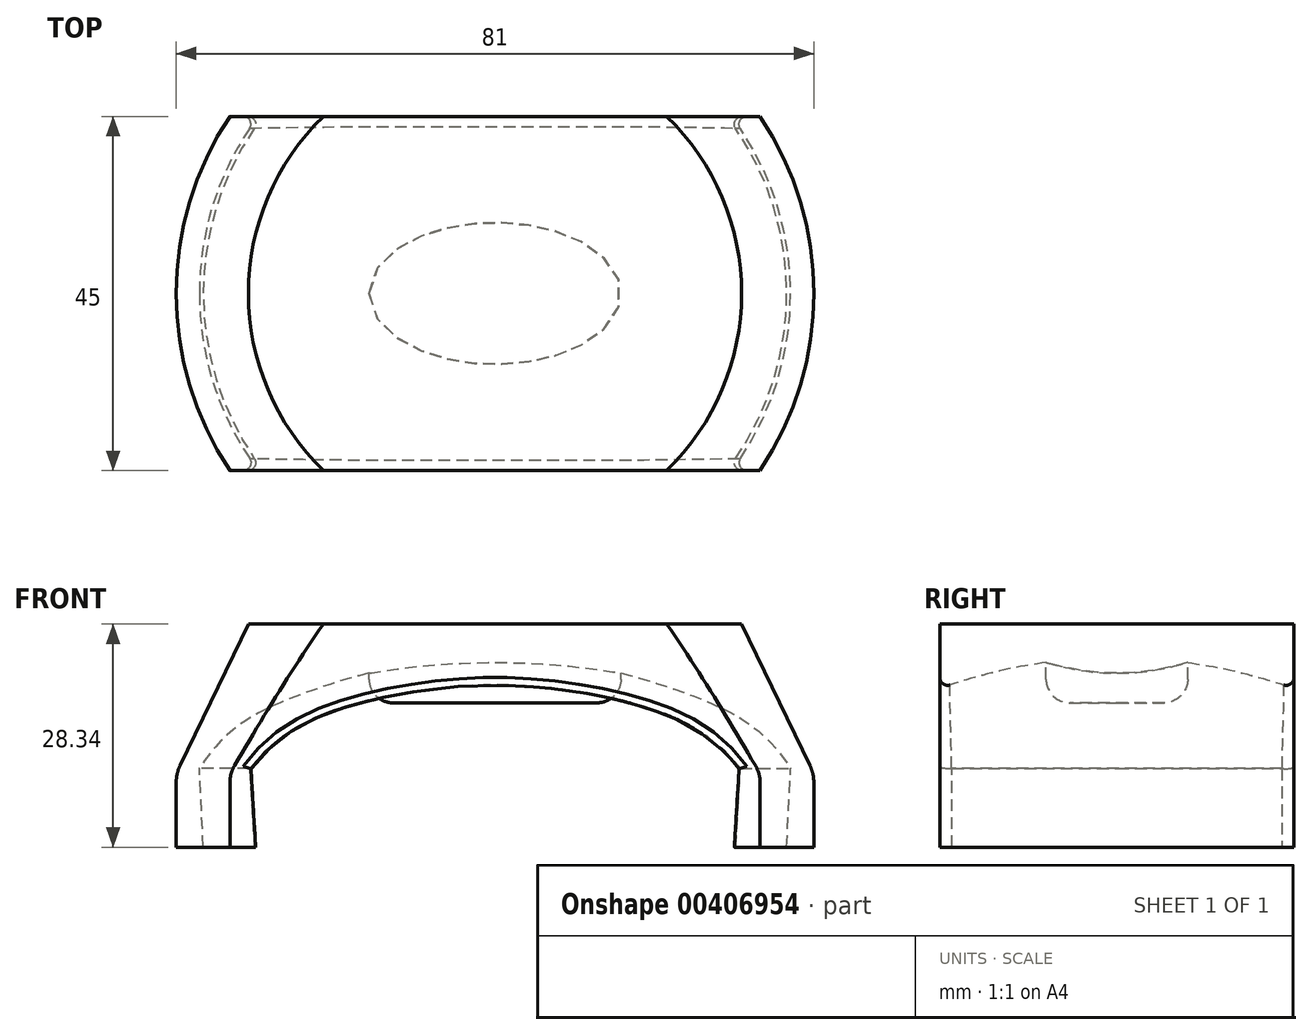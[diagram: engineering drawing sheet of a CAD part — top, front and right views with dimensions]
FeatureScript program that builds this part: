
annotation { "Feature Type Name" : "Feature", "Feature Type Description" : "" }
export const myFeature = defineFeature(function(context is Context, id is Id, definition is map)
    precondition{}
    {
        {
            var Q0;
            Q0=qCreatedBy(makeId("Top.planeOp"),FACE);
            var sketch = newSketch(context, id + "F0", { "sketchPlane" : qUnion([Q0])});
            skCircle(sketch, "E0", {"center": v(0, 0) * mm, "radius": 37.55 * mm});
            skSolve(sketch);
        }
        {
            var Q0;
            Q0=qCreatedBy(makeId("Front.planeOp"),FACE);
            var sketch = newSketch(context, id + "F1", { "sketchPlane" : qUnion([Q0])});
            skLineSegment(sketch, "E1", {"start": v(0, 0) * mm, "end": v(0, 14) * mm, "construction": true});
            skLineSegment(sketch, "E2", {"start": v(0, 0) * mm, "end": v(-37.56, 0) * mm, "construction": true});
            skFitSpline(sketch, "E3", {"points": [v(0, 14) * mm, v(-25.46, 9.08) * mm, v(-37.56, 0) * mm], "startDerivative": vector(-52.5, 1.08) * mm, "endDerivative": vector(-22.97, -35.71) * mm});
            skLineSegment(sketch, "E4", {"start": v(0, 14) * mm, "end": v(0, 18.34) * mm});
            skLineSegment(sketch, "E5", {"start": v(0, 18.34) * mm, "end": v(-31.33, 18.34) * mm});
            skLineSegment(sketch, "E6", {"start": v(-31.33, 18.34) * mm, "end": v(-40.5, -0.65) * mm});
            skLineSegment(sketch, "E7", {"start": v(-40.5, -0.65) * mm, "end": v(-40.5, -10) * mm});
            skLineSegment(sketch, "E8", {"start": v(-37.56, 0) * mm, "end": v(-37.56, -10) * mm});
            skLineSegment(sketch, "E9", {"start": v(-37.56, -10) * mm, "end": v(-37.06, -10) * mm});
            skLineSegment(sketch, "E10", {"start": v(-37.06, -10) * mm, "end": v(-37.56, 0) * mm});
            skLineSegment(sketch, "E11", {"start": v(-37.56, -10) * mm, "end": v(-40.5, -10) * mm});
            skLineSegment(sketch, "E12", {"start": v(-31.33, 18.34) * mm, "end": v(-39.17, 18.34) * mm, "construction": true});
            skSolve(sketch);
        }
        {
            var Q0;
            Q0=makeQuery(id+"F1.imprint","IMPRINT",FACE,{"disambiguationData":[TD([[makeQuery(id+"F1.imprint","IMPRINT",EDGE,{"derivedFrom":sQuery(id+"F1.wireOp",EDGE,"E3")}),-1.0]])]});
            var Q1;
            Q1=makeQuery(id+"F1.imprint","IMPRINT",FACE,{"disambiguationData":[TD([[makeQuery(id+"F1.imprint","IMPRINT",EDGE,{"derivedFrom":sQuery(id+"F1.wireOp",EDGE,"E8")}),1.0]])]});
            var Q2;
            Q2=sQuery(id+"F1.wireOp",EDGE,"E1");
            revolve(context, id + "F2", {"entities" : qUnion([Q0, Q1]), "axis" : qUnion([Q2]), "revolveType" : RevolveType.FULL});
        }
        {
            var Q0;
            Q0=qCreatedBy(makeId("Front.planeOp"),FACE);
            cPlane(context, id + "F3", {"entities" : qUnion([Q0]), "cplaneType" : CPlaneType.OFFSET, "offset" : 22.5 * mm, "width" : 150 * mm, "height" : 150 * mm});
        }
        {
            var Q0;
            Q0=qCreatedBy(id+"F3.planeOp",FACE);
            cPlane(context, id + "F4", {"entities" : qUnion([Q0]), "cplaneType" : CPlaneType.OFFSET, "offset" : 45 * mm, "oppositeDirection" : true, "width" : 150 * mm, "height" : 150 * mm});
        }
        {
            var Q0;
            Q0=qCreatedBy(id+"F3.planeOp",FACE);
            var sketch = newSketch(context, id + "F5", { "sketchPlane" : qUnion([Q0])});
            skLineSegment(sketch, "E13.bottom", {"start": v(-55.32, -24.65) * mm, "end": v(84.84, -24.65) * mm});
            skLineSegment(sketch, "E13.top", {"start": v(-55.32, 35.26) * mm, "end": v(84.84, 35.26) * mm});
            skLineSegment(sketch, "E13.left", {"start": v(-55.32, -24.65) * mm, "end": v(-55.32, 35.26) * mm});
            skLineSegment(sketch, "E13.right", {"start": v(84.84, -24.65) * mm, "end": v(84.84, 35.26) * mm});
            skSolve(sketch);
        }
        {
            var Q0;
            Q0 = qSketchRegion(id + "F5", true);
            extrude(context, id + "F6", {"entities" : qUnion([Q0]), "operationType" : NewBodyOperationType.REMOVE, "depth" : 25 * mm});
        }
        {
            var Q0;
            Q0=qCreatedBy(id+"F4.planeOp",FACE);
            var sketch = newSketch(context, id + "F7", { "sketchPlane" : qUnion([Q0])});
            skLineSegment(sketch, "E14.bottom", {"start": v(40.39, 27.93) * mm, "end": v(-45.5, 27.93) * mm});
            skLineSegment(sketch, "E14.top", {"start": v(40.39, -23.12) * mm, "end": v(-45.5, -23.12) * mm});
            skLineSegment(sketch, "E14.left", {"start": v(40.39, 27.93) * mm, "end": v(40.39, -23.12) * mm});
            skLineSegment(sketch, "E14.right", {"start": v(-45.5, 27.93) * mm, "end": v(-45.5, -23.12) * mm});
            skSolve(sketch);
        }
        {
            var Q0;
            Q0 = qSketchRegion(id + "F7", true);
            extrude(context, id + "F8", {"entities" : qUnion([Q0]), "operationType" : NewBodyOperationType.REMOVE, "oppositeDirection" : true, "depth" : 25 * mm});
        }
        {
            var Q0;
            Q0=makeQuery(id+"F2.opRevolve","SWEPT_FACE",FACE,{"disambiguationData":[OSD([sQuery(id+"F1.wireOp",EDGE,"E5")])]});
            var sketch = newSketch(context, id + "F9", { "sketchPlane" : qUnion([Q0])});
            skEllipse(sketch, "E15", {"center": v(0, 0) * mm, "majorRadius": 16 * mm, "minorRadius": 9 * mm, "majorAxis": v(-1, 0)});
            skSolve(sketch);
        }
        {
            var Q0;
            Q0=makeQuery(id+"F9.imprint","IMPRINT",FACE,{"disambiguationData":[TD([[makeQuery(id+"F9.imprint","IMPRINT",EDGE,{"derivedFrom":sQuery(id+"F9.wireOp",EDGE,"E15")}),1.0]])]});
            extrude(context, id + "F10", {"entities" : qUnion([Q0]), "operationType" : NewBodyOperationType.ADD, "oppositeDirection" : true, "depth" : 10 * mm});
        }
        {
            var Q0;
            Q0=makeQuery(id+"F10.opExtrude","CAP_EDGE",EDGE,{"disambiguationData":[OSD([sQuery(id+"F9.wireOp",EDGE,"E15")])],"isStart":false});
            fillet(context, id + "F11", {"entities" : qUnion([Q0]), "radius" : 3 * mm, "tangentPropagation" : true, "allowEdgeOverflow" : false});
        }
        {
            var Q0;
            Q0=makeQuery(id+"F8.boolean.opBoolean","SPLIT",EDGE,{"disambiguationData":[OD(0.0)],"derivedFrom":makeQuery(id+"F2.opRevolve","SWEPT_EDGE",EDGE,{"disambiguationData":[OSD([sQuery(id+"F1.wireOp",EDGE,"E6"),sQuery(id+"F1.wireOp",EDGE,"E7")])]})});
            var Q1;
            Q1=makeQuery(id+"F8.boolean.opBoolean","SPLIT",EDGE,{"disambiguationData":[OD(1.0)],"derivedFrom":makeQuery(id+"F2.opRevolve","SWEPT_EDGE",EDGE,{"disambiguationData":[OSD([sQuery(id+"F1.wireOp",EDGE,"E6"),sQuery(id+"F1.wireOp",EDGE,"E7")])]})});
            fillet(context, id + "F12", {"entities" : qUnion([Q0, Q1]), "radius" : 5 * mm, "tangentPropagation" : true, "allowEdgeOverflow" : false});
        }
        {
            var Q0;
            Q0=makeQuery(id+"F6.boolean.opBoolean","INTERSECT",EDGE,{"disambiguationData":[OD(1.0)],"derivedFrom":[makeQuery(id+"F2.opRevolve","SWEPT_FACE",FACE,{"disambiguationData":[OSD([sQuery(id+"F1.wireOp",EDGE,"E10")])]}),makeQuery(id+"F6.opExtrude","CAP_FACE",FACE,{"disambiguationData":[OSD([sQuery(id+"F5.wireOp",EDGE,"E13.bottom"),sQuery(id+"F5.wireOp",EDGE,"E13.top"),sQuery(id+"F5.wireOp",EDGE,"E13.left"),sQuery(id+"F5.wireOp",EDGE,"E13.right")])],"isStart":true})]});
            var Q1;
            Q1=makeQuery(id+"F6.boolean.opBoolean","INTERSECT",EDGE,{"disambiguationData":[OD(0.0)],"derivedFrom":[makeQuery(id+"F2.opRevolve","SWEPT_FACE",FACE,{"disambiguationData":[OSD([sQuery(id+"F1.wireOp",EDGE,"E10")])]}),makeQuery(id+"F6.opExtrude","CAP_FACE",FACE,{"disambiguationData":[OSD([sQuery(id+"F5.wireOp",EDGE,"E13.bottom"),sQuery(id+"F5.wireOp",EDGE,"E13.top"),sQuery(id+"F5.wireOp",EDGE,"E13.left"),sQuery(id+"F5.wireOp",EDGE,"E13.right")])],"isStart":true})]});
            var Q2;
            Q2=makeQuery(id+"F8.boolean.opBoolean","INTERSECT",EDGE,{"disambiguationData":[OD(0.0)],"derivedFrom":[makeQuery(id+"F2.opRevolve","SWEPT_FACE",FACE,{"disambiguationData":[OSD([sQuery(id+"F1.wireOp",EDGE,"E10")])]}),makeQuery(id+"F8.opExtrude","CAP_FACE",FACE,{"disambiguationData":[OSD([sQuery(id+"F7.wireOp",EDGE,"E14.bottom"),sQuery(id+"F7.wireOp",EDGE,"E14.top"),sQuery(id+"F7.wireOp",EDGE,"E14.left"),sQuery(id+"F7.wireOp",EDGE,"E14.right")])],"isStart":true})]});
            var Q3;
            Q3=makeQuery(id+"F8.boolean.opBoolean","INTERSECT",EDGE,{"disambiguationData":[OD(1.0)],"derivedFrom":[makeQuery(id+"F2.opRevolve","SWEPT_FACE",FACE,{"disambiguationData":[OSD([sQuery(id+"F1.wireOp",EDGE,"E10")])]}),makeQuery(id+"F8.opExtrude","CAP_FACE",FACE,{"disambiguationData":[OSD([sQuery(id+"F7.wireOp",EDGE,"E14.bottom"),sQuery(id+"F7.wireOp",EDGE,"E14.top"),sQuery(id+"F7.wireOp",EDGE,"E14.left"),sQuery(id+"F7.wireOp",EDGE,"E14.right")])],"isStart":true})]});
            var Q4;
            Q4=makeQuery(id+"F8.boolean.opBoolean","INTERSECT",EDGE,{"derivedFrom":[makeQuery(id+"F2.opRevolve","SWEPT_FACE",FACE,{"disambiguationData":[OSD([sQuery(id+"F1.wireOp",EDGE,"E3")])]}),makeQuery(id+"F8.opExtrude","CAP_FACE",FACE,{"disambiguationData":[OSD([sQuery(id+"F7.wireOp",EDGE,"E14.bottom"),sQuery(id+"F7.wireOp",EDGE,"E14.top"),sQuery(id+"F7.wireOp",EDGE,"E14.left"),sQuery(id+"F7.wireOp",EDGE,"E14.right")])],"isStart":true})]});
            var Q5;
            Q5=makeQuery(id+"F6.boolean.opBoolean","INTERSECT",EDGE,{"derivedFrom":[makeQuery(id+"F2.opRevolve","SWEPT_FACE",FACE,{"disambiguationData":[OSD([sQuery(id+"F1.wireOp",EDGE,"E3")])]}),makeQuery(id+"F6.opExtrude","CAP_FACE",FACE,{"disambiguationData":[OSD([sQuery(id+"F5.wireOp",EDGE,"E13.bottom"),sQuery(id+"F5.wireOp",EDGE,"E13.top"),sQuery(id+"F5.wireOp",EDGE,"E13.left"),sQuery(id+"F5.wireOp",EDGE,"E13.right")])],"isStart":true})]});
            fillet(context, id + "F13", {"entities" : qUnion([Q0, Q1, Q2, Q3, Q4, Q5]), "radius" : 1 * mm, "tangentPropagation" : true, "allowEdgeOverflow" : false});
        }
    });
